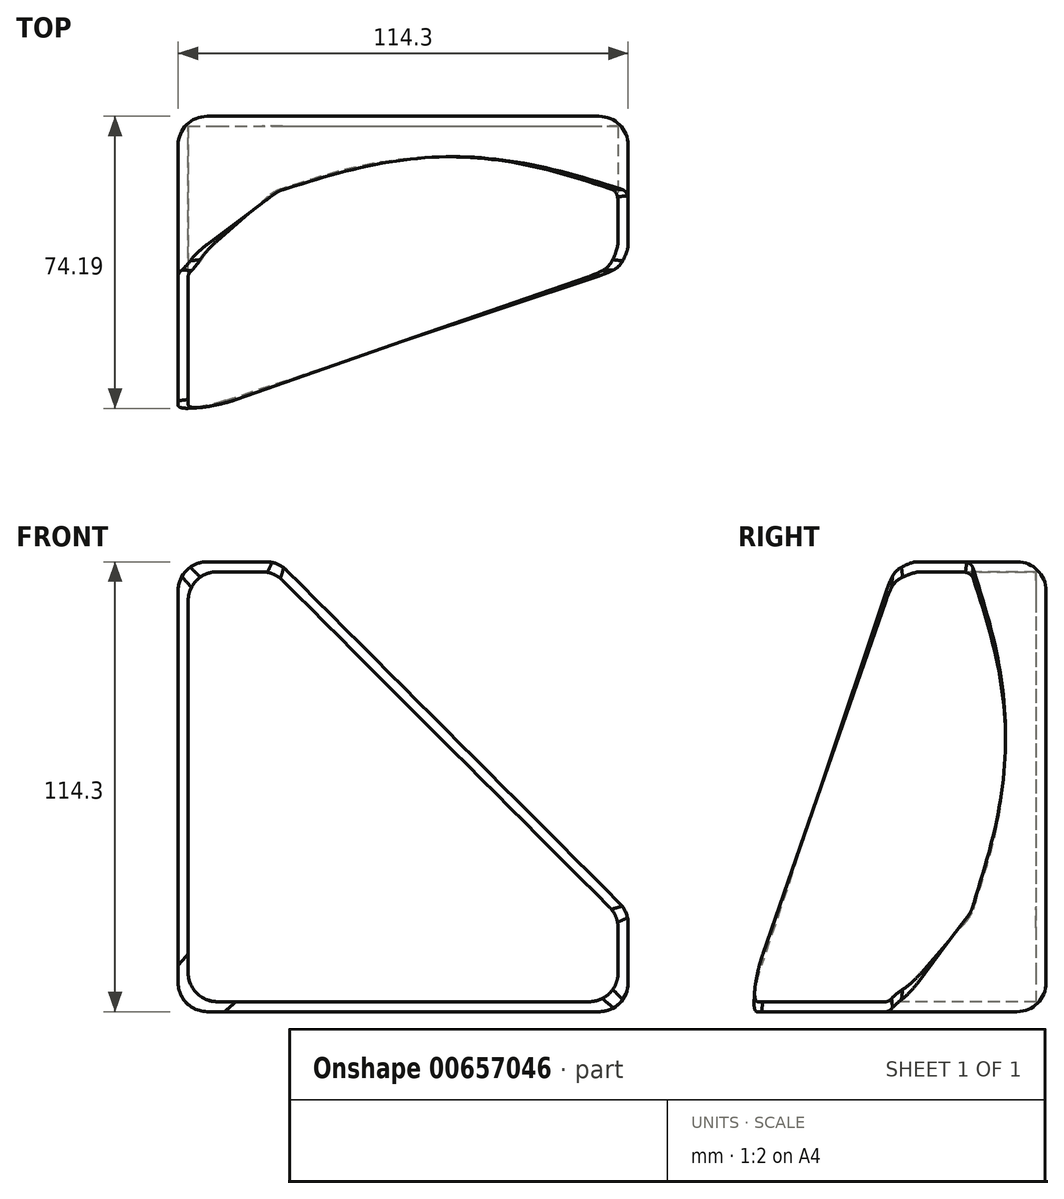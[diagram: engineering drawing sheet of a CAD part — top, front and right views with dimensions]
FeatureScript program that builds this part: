
annotation { "Feature Type Name" : "Feature", "Feature Type Description" : "" }
export const myFeature = defineFeature(function(context is Context, id is Id, definition is map)
    precondition{}
    {
        {
            var Q0;
            Q0=qCreatedBy(makeId("Front.planeOp"),FACE);
            var sketch = newSketch(context, id + "F0", { "sketchPlane" : qUnion([Q0])});
            skLineSegment(sketch, "E0", {"start": v(-114.3, 114.3) * mm, "end": v(-114.3, 0) * mm});
            skLineSegment(sketch, "E1", {"start": v(-114.3, 0) * mm, "end": v(0, 0) * mm});
            skLineSegment(sketch, "E2", {"start": v(-114.3, 114.3) * mm, "end": v(-88.9, 114.3) * mm});
            skLineSegment(sketch, "E3", {"start": v(-88.9, 114.3) * mm, "end": v(0, 25.4) * mm});
            skLineSegment(sketch, "E4", {"start": v(0, 25.4) * mm, "end": v(0, 0) * mm});
            skLineSegment(sketch, "E5.0", {"start": v(-89.95, 111.76) * mm, "end": v(-2.54, 24.35) * mm});
            skLineSegment(sketch, "E5.1", {"start": v(-111.76, 111.76) * mm, "end": v(-89.95, 111.76) * mm});
            skLineSegment(sketch, "E5.2", {"start": v(-2.54, 24.35) * mm, "end": v(-2.54, 2.54) * mm});
            skLineSegment(sketch, "E5.3", {"start": v(-111.76, 2.54) * mm, "end": v(-2.54, 2.54) * mm});
            skLineSegment(sketch, "E5.4", {"start": v(-111.76, 111.76) * mm, "end": v(-111.76, 2.54) * mm});
            skLineSegment(sketch, "E6", {"start": v(-114.3, 114.3) * mm, "end": v(-111.76, 111.76) * mm});
            skLineSegment(sketch, "E7", {"start": v(-88.9, 114.3) * mm, "end": v(-89.95, 111.76) * mm});
            skLineSegment(sketch, "E8", {"start": v(-2.54, 24.35) * mm, "end": v(0, 25.4) * mm});
            skLineSegment(sketch, "E9", {"start": v(0, 0) * mm, "end": v(-2.54, 2.54) * mm});
            skLineSegment(sketch, "E10", {"start": v(-111.76, 2.54) * mm, "end": v(-114.3, 0) * mm});
            skLineSegment(sketch, "E11", {"start": v(-24.25, 46.05) * mm, "end": v(-22.45, 47.85) * mm});
            skLineSegment(sketch, "E12", {"start": v(-66.45, 91.85) * mm, "end": v(-68.25, 90.05) * mm});
            skSolve(sketch);
        }
        {
            var Q0;
            Q0=sQuery(id+"F0.wireOp",EDGE,"E10");
            extrude(context, id + "F1", {"bodyType" : ToolBodyType.SURFACE, "surfaceEntities" : qUnion([Q0]), "depth" : 76.2 * mm, "offsetDistance" : 25.4 * mm});
        }
        {
            var Q0;
            Q0=sQuery(id+"F0.wireOp",EDGE,"E6");
            var Q1;
            Q1=sQuery(id+"F0.wireOp",EDGE,"E9");
            extrude(context, id + "F2", {"bodyType" : ToolBodyType.SURFACE, "surfaceEntities" : qUnion([Q0, Q1]), "depth" : 38.1 * mm, "offsetDistance" : 25.4 * mm});
        }
        {
            var Q0;
            Q0=sQuery(id+"F0.wireOp",EDGE,"E8");
            var Q1;
            Q1=sQuery(id+"F0.wireOp",EDGE,"E7");
            extrude(context, id + "F3", {"bodyType" : ToolBodyType.SURFACE, "surfaceEntities" : qUnion([Q0, Q1]), "depth" : 19.05 * mm, "offsetDistance" : 25.4 * mm});
        }
        {
            var Q0;
            Q0=sQuery(id+"F0.wireOp",EDGE,"E12");
            var Q1;
            Q1=sQuery(id+"F0.wireOp",EDGE,"E11");
            extrude(context, id + "F4", {"bodyType" : ToolBodyType.SURFACE, "surfaceEntities" : qUnion([Q0, Q1]), "depth" : 12.7 * mm, "offsetDistance" : 25.4 * mm});
        }
        {
            var Q0;
            Q0=makeQuery(id+"F2.opExtrude","SWEPT_BODY",BODY,{"disambiguationData":[OSD([sQuery(id+"F0.wireOp",EDGE,"E6")])]});
            var Q1;
            Q1=makeQuery(id+"F1.opExtrude","SWEPT_BODY",BODY,{"disambiguationData":[OSD([sQuery(id+"F0.wireOp",EDGE,"E10")])]});
            loft(context, id + "F5", {"sheetProfilesArray" : [{ "sheetProfileEntities" : qUnion([Q0]) }, { "sheetProfileEntities" : qUnion([Q1]) }]});
        }
        {
            var Q1;
            Q1=makeQuery(id+"F1.opExtrude","SWEPT_BODY",BODY,{"disambiguationData":[OSD([sQuery(id+"F0.wireOp",EDGE,"E10")])]});
            var Q2;
            Q2=makeQuery(id+"F2.opExtrude","SWEPT_BODY",BODY,{"disambiguationData":[OSD([sQuery(id+"F0.wireOp",EDGE,"E9")])]});
            loft(context, id + "F6", {"operationType" : NewBodyOperationType.ADD, "sheetProfilesArray" : [{ "sheetProfileEntities" : qUnion([Q1]) }, { "sheetProfileEntities" : qUnion([Q2]) }]});
        }
        {
            var Q1;
            Q1=makeQuery(id+"F2.opExtrude","SWEPT_FACE",FACE,{"disambiguationData":[OSD([sQuery(id+"F0.wireOp",EDGE,"E9")])]});
            var Q2;
            Q2=makeQuery(id+"F3.opExtrude","SWEPT_BODY",BODY,{"disambiguationData":[OSD([sQuery(id+"F0.wireOp",EDGE,"E8")])]});
            loft(context, id + "F7", {"operationType" : NewBodyOperationType.ADD, "sheetProfilesArray" : [{ "sheetProfileEntities" : qUnion([Q1]) }, { "sheetProfileEntities" : qUnion([Q2]) }]});
        }
        {
            var Q1;
            Q1=makeQuery(id+"F2.opExtrude","SWEPT_FACE",FACE,{"disambiguationData":[OSD([sQuery(id+"F0.wireOp",EDGE,"E6")])]});
            var Q2;
            Q2=makeQuery(id+"F3.opExtrude","SWEPT_BODY",BODY,{"disambiguationData":[OSD([sQuery(id+"F0.wireOp",EDGE,"E7")])]});
            loft(context, id + "F8", {"operationType" : NewBodyOperationType.ADD, "sheetProfilesArray" : [{ "sheetProfileEntities" : qUnion([Q1]) }, { "sheetProfileEntities" : qUnion([Q2]) }]});
        }
        {
            var Q1;
            Q1=makeQuery(id+"F3.opExtrude","SWEPT_BODY",BODY,{"disambiguationData":[OSD([sQuery(id+"F0.wireOp",EDGE,"E8")])]});
            var Q2;
            Q2=makeQuery(id+"F4.opExtrude","SWEPT_BODY",BODY,{"disambiguationData":[OSD([sQuery(id+"F0.wireOp",EDGE,"E11")])]});
            var Q3;
            Q3=makeQuery(id+"F4.opExtrude","SWEPT_BODY",BODY,{"disambiguationData":[OSD([sQuery(id+"F0.wireOp",EDGE,"E12")])]});
            var Q4;
            Q4=makeQuery(id+"F3.opExtrude","SWEPT_BODY",BODY,{"disambiguationData":[OSD([sQuery(id+"F0.wireOp",EDGE,"E7")])]});
            loft(context, id + "F9", {"operationType" : NewBodyOperationType.ADD, "sheetProfilesArray" : [{ "sheetProfileEntities" : qUnion([Q1]) }, { "sheetProfileEntities" : qUnion([Q2]) }, { "sheetProfileEntities" : qUnion([Q3]) }, { "sheetProfileEntities" : qUnion([Q4]) }]});
        }
        {
            var Q0;
            {var subQ0=sQuery(id+"F0.wireOp",EDGE,"E5.1");Q0=makeQuery(id+"F0.imprint","IMPRINT",FACE,{"disambiguationData":[TD([[makeQuery(id+"F0.imprint","IMPRINT",EDGE,{"derivedFrom":subQ0}),-1.0]])]});}
            extrude(context, id + "F10", {"entities" : qUnion([Q0]), "operationType" : NewBodyOperationType.ADD, "depth" : 2.54 * mm, "offsetDistance" : 25.4 * mm});
        }
        {
            var Q0;
            {var subQ0=sQuery(id+"F0.wireOp",VERTEX,"E6.end");Q0=makeQuery(id+"F8.boolean.opBoolean","MERGE",EDGE,{"derivedFrom":[makeQuery(id+"F5.opLoft","MID_CAP_EDGE",EDGE,{"disambiguationData":[OSD([subQ0])],"capPos":0.0}),makeQuery(id+"F8.opLoft","MID_CAP_EDGE",EDGE,{"disambiguationData":[OSD([subQ0])],"capPos":0.0})]});}
            var Q1;
            {var subQ0=sQuery(id+"F0.wireOp",VERTEX,"E7.end");Q1=makeQuery(id+"F9.boolean.opBoolean","MERGE",EDGE,{"derivedFrom":[makeQuery(id+"F8.opLoft","MID_CAP_EDGE",EDGE,{"disambiguationData":[OSD([subQ0])],"capPos":1.0}),makeQuery(id+"F9.opLoft","MID_CAP_EDGE",EDGE,{"disambiguationData":[OSD([subQ0])],"capPos":3.0})]});}
            var Q2;
            {var subQ0=sQuery(id+"F0.wireOp",VERTEX,"E8.start");Q2=makeQuery(id+"F9.boolean.opBoolean","MERGE",EDGE,{"derivedFrom":[makeQuery(id+"F7.opLoft","MID_CAP_EDGE",EDGE,{"disambiguationData":[OSD([subQ0])],"capPos":1.0}),makeQuery(id+"F9.opLoft","MID_CAP_EDGE",EDGE,{"disambiguationData":[OSD([subQ0])],"capPos":0.0})]});}
            var Q3;
            {var subQ0=sQuery(id+"F0.wireOp",VERTEX,"E9.end");Q3=makeQuery(id+"F7.boolean.opBoolean","MERGE",EDGE,{"derivedFrom":[makeQuery(id+"F6.opLoft","MID_CAP_EDGE",EDGE,{"disambiguationData":[OSD([subQ0])],"capPos":1.0}),makeQuery(id+"F7.opLoft","MID_CAP_EDGE",EDGE,{"disambiguationData":[OSD([subQ0])],"capPos":0.0})]});}
            var Q4;
            {var subQ0=sQuery(id+"F0.wireOp",VERTEX,"E9.start");Q4=makeQuery(id+"F7.boolean.opBoolean","MERGE",EDGE,{"derivedFrom":[makeQuery(id+"F6.opLoft","MID_CAP_EDGE",EDGE,{"disambiguationData":[OSD([subQ0])],"capPos":1.0}),makeQuery(id+"F7.opLoft","MID_CAP_EDGE",EDGE,{"disambiguationData":[OSD([subQ0])],"capPos":0.0})]});}
            var Q5;
            {var subQ0=sQuery(id+"F0.wireOp",VERTEX,"E8.end");Q5=makeQuery(id+"F9.boolean.opBoolean","MERGE",EDGE,{"derivedFrom":[makeQuery(id+"F7.opLoft","MID_CAP_EDGE",EDGE,{"disambiguationData":[OSD([subQ0])],"capPos":1.0}),makeQuery(id+"F9.opLoft","MID_CAP_EDGE",EDGE,{"disambiguationData":[OSD([subQ0])],"capPos":0.0})]});}
            var Q6;
            {var subQ0=sQuery(id+"F0.wireOp",VERTEX,"E7.start");Q6=makeQuery(id+"F9.boolean.opBoolean","MERGE",EDGE,{"derivedFrom":[makeQuery(id+"F8.opLoft","MID_CAP_EDGE",EDGE,{"disambiguationData":[OSD([subQ0])],"capPos":1.0}),makeQuery(id+"F9.opLoft","MID_CAP_EDGE",EDGE,{"disambiguationData":[OSD([subQ0])],"capPos":3.0})]});}
            var Q7;
            {var subQ0=sQuery(id+"F0.wireOp",VERTEX,"E6.start");Q7=makeQuery(id+"F8.boolean.opBoolean","MERGE",EDGE,{"derivedFrom":[makeQuery(id+"F5.opLoft","MID_CAP_EDGE",EDGE,{"disambiguationData":[OSD([subQ0])],"capPos":0.0}),makeQuery(id+"F8.opLoft","MID_CAP_EDGE",EDGE,{"disambiguationData":[OSD([subQ0])],"capPos":0.0})]});}
            fillet(context, id + "F11", {"entities" : qUnion([Q0, Q1, Q2, Q3, Q4, Q5, Q6, Q7]), "radius" : 7.36 * mm, "tangentPropagation" : true, "allowEdgeOverflow" : false});
        }
        {
            var Q0;
            {var subQ0=sQuery(id+"F0.wireOp",VERTEX,"E9.start");var subQ1=sQuery(id+"F0.wireOp",VERTEX,"E10.end");Q0=makeQuery(id+"F6.opLoft","SWEPT_EDGE",EDGE,{"disambiguationData":[OSD([subQ0,subQ1]),TDD([makeQuery(id+"F1.opExtrude","CAP_VERTEX",VERTEX,{"disambiguationData":[OSD([subQ1])],"isStart":true}),makeQuery(id+"F2.opExtrude","CAP_VERTEX",VERTEX,{"disambiguationData":[OSD([subQ0])],"isStart":true})])]});}
            var Q1;
            {var subQ0=sQuery(id+"F0.wireOp",VERTEX,"E6.start");var subQ1=sQuery(id+"F0.wireOp",VERTEX,"E10.end");Q1=makeQuery(id+"F5.opLoft","SWEPT_EDGE",EDGE,{"disambiguationData":[OSD([subQ0,subQ1]),TDD([makeQuery(id+"F1.opExtrude","CAP_VERTEX",VERTEX,{"disambiguationData":[OSD([subQ1])],"isStart":true}),makeQuery(id+"F2.opExtrude","CAP_VERTEX",VERTEX,{"disambiguationData":[OSD([subQ0])],"isStart":true})])]});}
            var Q2;
            {var subQ0=sQuery(id+"F0.wireOp",VERTEX,"E10.end");Q2=makeQuery(id+"F6.boolean.opBoolean","MERGE",EDGE,{"derivedFrom":[makeQuery(id+"F5.opLoft","MID_CAP_EDGE",EDGE,{"disambiguationData":[OSD([subQ0])],"capPos":1.0}),makeQuery(id+"F6.opLoft","MID_CAP_EDGE",EDGE,{"disambiguationData":[OSD([subQ0])],"capPos":0.0})]});}
            var Q3;
            Q3=makeQuery(id+"F10.opExtrude","CAP_EDGE",EDGE,{"disambiguationData":[OSD([sQuery(id+"F0.wireOp",EDGE,"E5.4")])],"isStart":false});
            var Q4;
            Q4=makeQuery(id+"F10.opExtrude","CAP_EDGE",EDGE,{"disambiguationData":[OSD([sQuery(id+"F0.wireOp",EDGE,"E5.3")])],"isStart":false});
            var Q5;
            {var subQ0=sQuery(id+"F0.wireOp",VERTEX,"E10.start");Q5=makeQuery(id+"F6.boolean.opBoolean","MERGE",EDGE,{"derivedFrom":[makeQuery(id+"F5.opLoft","MID_CAP_EDGE",EDGE,{"disambiguationData":[OSD([subQ0])],"capPos":1.0}),makeQuery(id+"F6.opLoft","MID_CAP_EDGE",EDGE,{"disambiguationData":[OSD([subQ0])],"capPos":0.0})]});}
            fillet(context, id + "F12", {"entities" : qUnion([Q0, Q1, Q2, Q3, Q4, Q5]), "radius" : 7.36 * mm, "tangentPropagation" : true, "allowEdgeOverflow" : false});
        }
        {
            var Q0;
            {var subQ0=sQuery(id+"F0.wireOp",EDGE,"E10");var subQ1=makeQuery(id+"F1.opExtrude","CAP_EDGE",EDGE,{"disambiguationData":[OSD([subQ0])],"isStart":false});var subQ2=sQuery(id+"F0.wireOp",VERTEX,"E10.end");var subQ3=makeQuery(id+"F1.opExtrude","CAP_VERTEX",VERTEX,{"disambiguationData":[OSD([subQ2])],"isStart":false});var subQ4=sQuery(id+"F0.wireOp",VERTEX,"E10.start");var subQ5=makeQuery(id+"F1.opExtrude","CAP_VERTEX",VERTEX,{"disambiguationData":[OSD([subQ4])],"isStart":false});Q0=makeQuery(id+"F6.boolean.opBoolean","MERGE",EDGE,{"derivedFrom":[makeQuery(id+"F5.opLoft","MID_CAP_EDGE",EDGE,{"disambiguationData":[OSD([subQ4,subQ2,subQ0]),TDD([subQ5,subQ3,subQ1])],"capPos":1.0}),makeQuery(id+"F6.opLoft","MID_CAP_EDGE",EDGE,{"disambiguationData":[OSD([subQ4,subQ2,subQ0]),TDD([subQ5,subQ3,subQ1])],"capPos":0.0})]});}
            fillet(context, id + "F13", {"entities" : qUnion([Q0]), "radius" : 21.48 * mm, "tangentPropagation" : true, "allowEdgeOverflow" : false});
        }
        {
            var Q0;
            {var subQ0=sQuery(id+"F0.wireOp",EDGE,"E9");var subQ1=makeQuery(id+"F2.opExtrude","CAP_EDGE",EDGE,{"disambiguationData":[OSD([subQ0])],"isStart":false});var subQ2=sQuery(id+"F0.wireOp",VERTEX,"E9.end");var subQ3=makeQuery(id+"F2.opExtrude","CAP_VERTEX",VERTEX,{"disambiguationData":[OSD([subQ2])],"isStart":false});var subQ4=sQuery(id+"F0.wireOp",VERTEX,"E9.start");var subQ5=makeQuery(id+"F2.opExtrude","CAP_VERTEX",VERTEX,{"disambiguationData":[OSD([subQ4])],"isStart":false});Q0=makeQuery(id+"F7.boolean.opBoolean","MERGE",EDGE,{"derivedFrom":[makeQuery(id+"F6.opLoft","MID_CAP_EDGE",EDGE,{"disambiguationData":[OSD([subQ4,subQ2,subQ0]),TDD([subQ5,subQ3,subQ1])],"capPos":1.0}),makeQuery(id+"F7.opLoft","MID_CAP_EDGE",EDGE,{"disambiguationData":[OSD([subQ4,subQ2,subQ0]),TDD([subQ5,subQ3,subQ1])],"capPos":0.0})]});}
            var Q1;
            {var subQ0=sQuery(id+"F0.wireOp",EDGE,"E6");var subQ1=makeQuery(id+"F2.opExtrude","CAP_EDGE",EDGE,{"disambiguationData":[OSD([subQ0])],"isStart":false});var subQ2=sQuery(id+"F0.wireOp",VERTEX,"E6.end");var subQ3=makeQuery(id+"F2.opExtrude","CAP_VERTEX",VERTEX,{"disambiguationData":[OSD([subQ2])],"isStart":false});var subQ4=sQuery(id+"F0.wireOp",VERTEX,"E6.start");var subQ5=makeQuery(id+"F2.opExtrude","CAP_VERTEX",VERTEX,{"disambiguationData":[OSD([subQ4])],"isStart":false});Q1=makeQuery(id+"F8.boolean.opBoolean","MERGE",EDGE,{"derivedFrom":[makeQuery(id+"F5.opLoft","MID_CAP_EDGE",EDGE,{"disambiguationData":[OSD([subQ4,subQ2,subQ0]),TDD([subQ5,subQ3,subQ1])],"capPos":0.0}),makeQuery(id+"F8.opLoft","MID_CAP_EDGE",EDGE,{"disambiguationData":[OSD([subQ4,subQ2,subQ0]),TDD([subQ5,subQ3,subQ1])],"capPos":0.0})]});}
            fillet(context, id + "F14", {"entities" : qUnion([Q0, Q1]), "radius" : 9.77 * mm, "tangentPropagation" : true, "allowEdgeOverflow" : false});
        }
        {
            var Q0;
            {var subQ0=sQuery(id+"F0.wireOp",EDGE,"E8");var subQ1=makeQuery(id+"F3.opExtrude","CAP_EDGE",EDGE,{"disambiguationData":[OSD([subQ0])],"isStart":false});var subQ2=sQuery(id+"F0.wireOp",VERTEX,"E8.end");var subQ3=makeQuery(id+"F3.opExtrude","CAP_VERTEX",VERTEX,{"disambiguationData":[OSD([subQ2])],"isStart":false});var subQ4=sQuery(id+"F0.wireOp",VERTEX,"E8.start");var subQ5=makeQuery(id+"F3.opExtrude","CAP_VERTEX",VERTEX,{"disambiguationData":[OSD([subQ4])],"isStart":false});Q0=makeQuery(id+"F9.boolean.opBoolean","MERGE",EDGE,{"derivedFrom":[makeQuery(id+"F7.opLoft","MID_CAP_EDGE",EDGE,{"disambiguationData":[OSD([subQ4,subQ2,subQ0]),TDD([subQ5,subQ3,subQ1])],"capPos":1.0}),makeQuery(id+"F9.opLoft","MID_CAP_EDGE",EDGE,{"disambiguationData":[OSD([subQ4,subQ2,subQ0]),TDD([subQ5,subQ3,subQ1])],"capPos":0.0})]});}
            var Q1;
            {var subQ0=sQuery(id+"F0.wireOp",EDGE,"E7");var subQ1=makeQuery(id+"F3.opExtrude","CAP_EDGE",EDGE,{"disambiguationData":[OSD([subQ0])],"isStart":false});var subQ2=sQuery(id+"F0.wireOp",VERTEX,"E7.end");var subQ3=makeQuery(id+"F3.opExtrude","CAP_VERTEX",VERTEX,{"disambiguationData":[OSD([subQ2])],"isStart":false});var subQ4=sQuery(id+"F0.wireOp",VERTEX,"E7.start");var subQ5=makeQuery(id+"F3.opExtrude","CAP_VERTEX",VERTEX,{"disambiguationData":[OSD([subQ4])],"isStart":false});Q1=makeQuery(id+"F9.boolean.opBoolean","MERGE",EDGE,{"derivedFrom":[makeQuery(id+"F8.opLoft","MID_CAP_EDGE",EDGE,{"disambiguationData":[OSD([subQ4,subQ2,subQ0]),TDD([subQ5,subQ3,subQ1])],"capPos":1.0}),makeQuery(id+"F9.opLoft","MID_CAP_EDGE",EDGE,{"disambiguationData":[OSD([subQ4,subQ2,subQ0]),TDD([subQ5,subQ3,subQ1])],"capPos":3.0})]});}
            fillet(context, id + "F15", {"entities" : qUnion([Q0, Q1]), "radius" : 8.2 * mm, "tangentPropagation" : true, "allowEdgeOverflow" : false});
        }
    });
